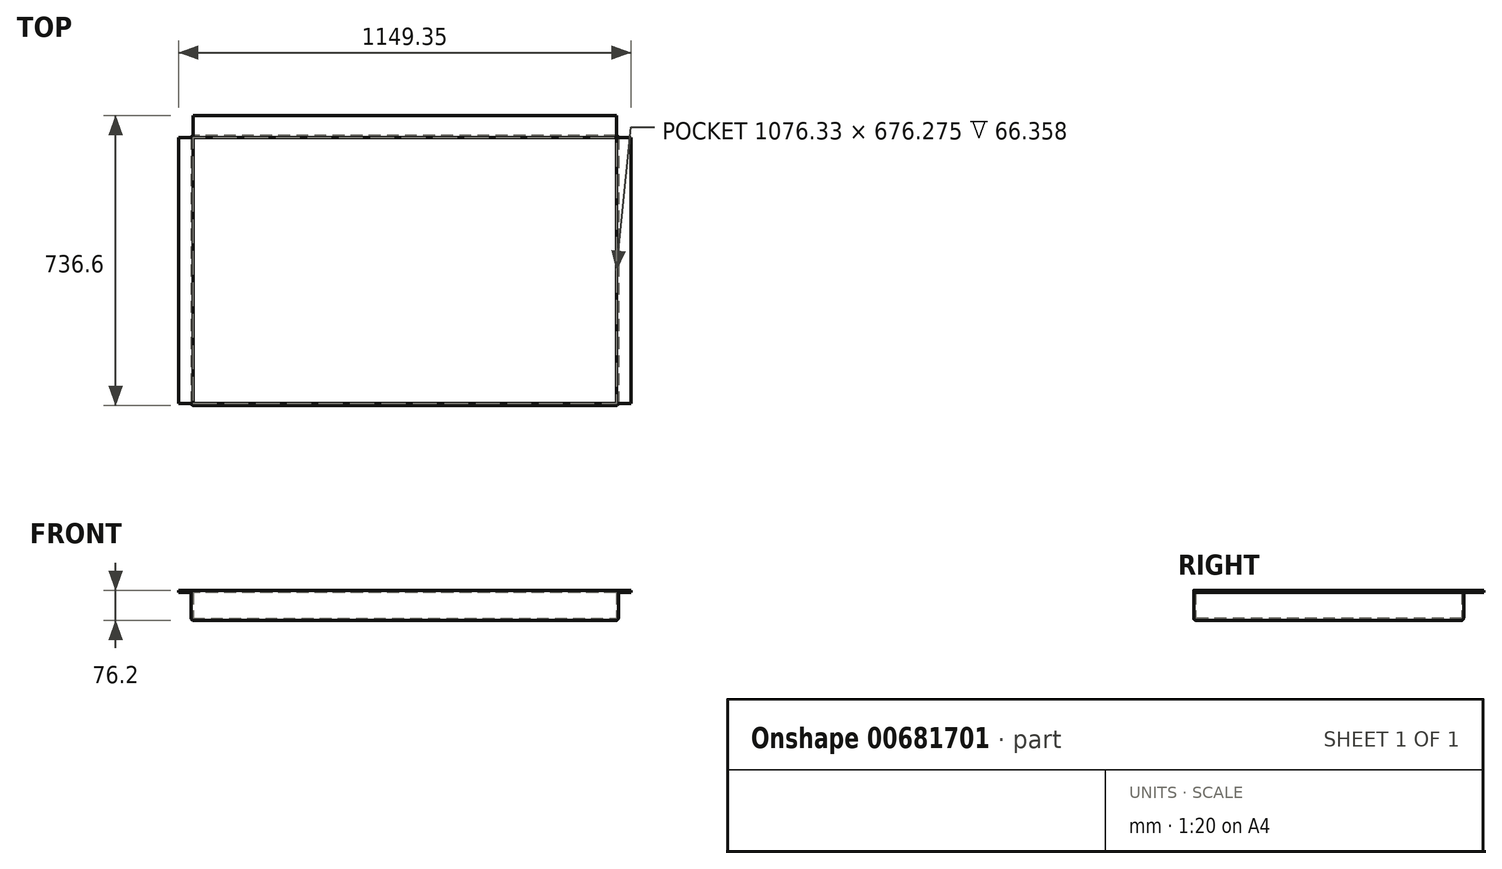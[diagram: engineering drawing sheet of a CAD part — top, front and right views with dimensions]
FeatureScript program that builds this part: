
annotation { "Feature Type Name" : "Feature", "Feature Type Description" : "" }
export const myFeature = defineFeature(function(context is Context, id is Id, definition is map)
    precondition{}
    {
        {
            var Q0;
            Q0=qCreatedBy(makeId("Top.planeOp"),FACE);
            var sketch = newSketch(context, id + "F0", { "sketchPlane" : qUnion([Q0])});
            skLineSegment(sketch, "E0.bottom", {"start": v(-1085.85, 685.8) * mm, "end": v(0, 685.8) * mm});
            skLineSegment(sketch, "E0.top", {"start": v(-1085.85, 0) * mm, "end": v(0, 0) * mm});
            skLineSegment(sketch, "E0.left", {"start": v(-1085.85, 685.8) * mm, "end": v(-1085.85, 0) * mm});
            skLineSegment(sketch, "E0.right", {"start": v(0, 685.8) * mm, "end": v(0, 0) * mm});
            skSolve(sketch);
        }
        {
            var Q0;
            Q0=makeQuery(id+"F0.imprint","IMPRINT",FACE,{"disambiguationData":[TD([[makeQuery(id+"F0.imprint","IMPRINT",EDGE,{"derivedFrom":sQuery(id+"F0.wireOp",EDGE,"E0.bottom")}),-1.0]])]});
            extrude(context, id + "F1", {"entities" : qUnion([Q0]), "depth" : 76.2 * mm, "offsetDistance" : 25.4 * mm});
        }
        {
            var Q0;
            Q0=makeQuery(id+"F8.boolean.opBoolean","MERGE",FACE,{"derivedFrom":[makeQuery(id+"F6.boolean.opBoolean","MERGE",FACE,{"derivedFrom":[makeQuery(id+"F4.boolean.opBoolean","MERGE",FACE,{"derivedFrom":[makeQuery(id+"F1.opExtrude","CAP_FACE",FACE,{"disambiguationData":[OSD([sQuery(id+"F0.wireOp",EDGE,"E0.bottom"),sQuery(id+"F0.wireOp",EDGE,"E0.top"),sQuery(id+"F0.wireOp",EDGE,"E0.left"),sQuery(id+"F0.wireOp",EDGE,"E0.right")])],"isStart":false}),makeQuery(id+"F4.opExtrude","SWEPT_FACE",FACE,{"disambiguationData":[OSD([sQuery(id+"F3.wireOp",EDGE,"44d1248c-61a8-45d5-8632-d3e4858e4744.0.2")])]})]}),makeQuery(id+"F6.opExtrude","SWEPT_FACE",FACE,{"disambiguationData":[OSD([sQuery(id+"F5.wireOp",EDGE,"3c0d171c-9aaa-4276-868c-e9e233a4677e.0.2")])]})]}),makeQuery(id+"F8.opExtrude","SWEPT_FACE",FACE,{"disambiguationData":[OSD([sQuery(id+"F7.wireOp",EDGE,"b2a400e3-6624-437d-8caf-46d41290d6b5.1.7")])]})]});
            shell(context, id + "F2", {"entities" : qUnion([Q0]), "thickness" : 4.76 * mm});
        }
        {
            var Q0;
            Q0=makeQuery(id+"F1.opExtrude","SWEPT_FACE",FACE,{"disambiguationData":[OSD([sQuery(id+"F0.wireOp",EDGE,"E0.left")])]});
            var sketch = newSketch(context, id + "F3", { "sketchPlane" : qUnion([Q0])});
            skLineSegment(sketch, "E1.0.0", {"start": v(-4.76, 4.76) * mm, "end": v(-681.04, 4.76) * mm});
            skLineSegment(sketch, "E1.0.1", {"start": v(-681.04, 4.76) * mm, "end": v(-681.04, 76.2) * mm});
            skLineSegment(sketch, "E1.0.2", {"start": v(-681.04, 76.2) * mm, "end": v(-4.76, 76.2) * mm});
            skLineSegment(sketch, "E1.0.3", {"start": v(-4.76, 76.2) * mm, "end": v(-4.76, 4.76) * mm});
            skLineSegment(sketch, "E2", {"start": v(-681.04, 71.44) * mm, "end": v(-4.76, 71.44) * mm});
            skSolve(sketch);
        }
        {
            var Q0;
            {var subQ0=sQuery(id+"F3.wireOp",EDGE,"E1.0.2");Q0=makeQuery(id+"F3.imprint","IMPRINT",FACE,{"disambiguationData":[TD([[makeQuery(id+"F3.imprint","IMPRINT",EDGE,{"derivedFrom":subQ0}),-1.0]])]});}
            extrude(context, id + "F4", {"entities" : qUnion([Q0]), "operationType" : NewBodyOperationType.ADD, "depth" : 31.75 * mm, "offsetDistance" : 25.4 * mm});
        }
        {
            var Q0;
            Q0=makeQuery(id+"F1.opExtrude","SWEPT_FACE",FACE,{"disambiguationData":[OSD([sQuery(id+"F0.wireOp",EDGE,"E0.right")])]});
            var sketch = newSketch(context, id + "F5", { "sketchPlane" : qUnion([Q0])});
            skLineSegment(sketch, "E3.0.0", {"start": v(681.04, 4.76) * mm, "end": v(4.76, 4.76) * mm});
            skLineSegment(sketch, "E3.0.1", {"start": v(4.76, 4.76) * mm, "end": v(4.76, 76.2) * mm});
            skLineSegment(sketch, "E3.0.2", {"start": v(4.76, 76.2) * mm, "end": v(681.04, 76.2) * mm});
            skLineSegment(sketch, "E3.0.3", {"start": v(681.04, 76.2) * mm, "end": v(681.04, 4.76) * mm});
            skLineSegment(sketch, "E4", {"start": v(4.76, 71.44) * mm, "end": v(681.04, 71.44) * mm});
            skPoint(sketch, "E4.endSnap0", {"position": v(681.04, 40.48) * mm});
            skSolve(sketch);
        }
        {
            var Q0;
            {var subQ0=sQuery(id+"F5.wireOp",EDGE,"E3.0.2");Q0=makeQuery(id+"F5.imprint","IMPRINT",FACE,{"disambiguationData":[TD([[makeQuery(id+"F5.imprint","IMPRINT",EDGE,{"derivedFrom":subQ0}),1.0]])]});}
            extrude(context, id + "F6", {"entities" : qUnion([Q0]), "operationType" : NewBodyOperationType.ADD, "depth" : 31.75 * mm, "offsetDistance" : 25.4 * mm});
        }
        {
            var Q0;
            Q0=makeQuery(id+"F1.opExtrude","SWEPT_FACE",FACE,{"disambiguationData":[OSD([sQuery(id+"F0.wireOp",EDGE,"E0.bottom")])]});
            var sketch = newSketch(context, id + "F7", { "sketchPlane" : qUnion([Q0])});
            skLineSegment(sketch, "E5.0.0", {"start": v(1081.09, 4.76) * mm, "end": v(4.76, 4.76) * mm});
            skLineSegment(sketch, "E5.0.1", {"start": v(4.76, 4.76) * mm, "end": v(4.76, 76.2) * mm});
            skLineSegment(sketch, "E5.0.2", {"start": v(4.76, 76.2) * mm, "end": v(1081.09, 76.2) * mm});
            skLineSegment(sketch, "E5.0.3", {"start": v(1081.09, 76.2) * mm, "end": v(1081.09, 4.76) * mm});
            skLineSegment(sketch, "E6", {"start": v(4.76, 71.44) * mm, "end": v(1081.09, 71.44) * mm});
            skSolve(sketch);
        }
        {
            var Q0;
            {var subQ0=sQuery(id+"F7.wireOp",EDGE,"E5.0.2");Q0=makeQuery(id+"F7.imprint","IMPRINT",FACE,{"disambiguationData":[TD([[makeQuery(id+"F7.imprint","IMPRINT",EDGE,{"derivedFrom":subQ0}),1.0]])]});}
            extrude(context, id + "F8", {"entities" : qUnion([Q0]), "operationType" : NewBodyOperationType.ADD, "depth" : 50.8 * mm, "offsetDistance" : 25.4 * mm});
        }
        {
            var Q0;
            Q0=makeQuery(id+"F1.opExtrude","CAP_FACE",FACE,{"disambiguationData":[OSD([sQuery(id+"F0.wireOp",EDGE,"E0.bottom"),sQuery(id+"F0.wireOp",EDGE,"E0.top"),sQuery(id+"F0.wireOp",EDGE,"E0.left"),sQuery(id+"F0.wireOp",EDGE,"E0.right")])],"isStart":true});
            var Q1;
            Q1=makeQuery(id+"F1.opExtrude","SWEPT_EDGE",EDGE,{"disambiguationData":[OSD([sQuery(id+"F0.wireOp",EDGE,"E0.bottom"),sQuery(id+"F0.wireOp",EDGE,"E0.left")])]});
            var Q2;
            Q2=makeQuery(id+"F1.opExtrude","SWEPT_EDGE",EDGE,{"disambiguationData":[OSD([sQuery(id+"F0.wireOp",EDGE,"E0.top"),sQuery(id+"F0.wireOp",EDGE,"E0.left")])]});
            var Q3;
            Q3=makeQuery(id+"F1.opExtrude","SWEPT_EDGE",EDGE,{"disambiguationData":[OSD([sQuery(id+"F0.wireOp",EDGE,"E0.top"),sQuery(id+"F0.wireOp",EDGE,"E0.right")])]});
            var Q4;
            Q4=makeQuery(id+"F1.opExtrude","SWEPT_EDGE",EDGE,{"disambiguationData":[OSD([sQuery(id+"F0.wireOp",EDGE,"E0.bottom"),sQuery(id+"F0.wireOp",EDGE,"E0.right")])]});
            fillet(context, id + "F9", {"entities" : qUnion([Q0, Q1, Q2, Q3, Q4]), "radius" : 6.35 * mm, "tangentPropagation" : true, "allowEdgeOverflow" : false});
        }
        {
            var Q0;
            {var subQ0=sQuery(id+"F0.wireOp",EDGE,"E0.bottom");Q0=makeQuery(id+"F2.opShell","OFFSET_EDGE",EDGE,{"disambiguationData":[OSD([subQ0]),TDD([makeQuery(id+"F1.opExtrude","CAP_EDGE",EDGE,{"disambiguationData":[OSD([subQ0])],"isStart":false})])]});}
            var Q1;
            {var subQ0=sQuery(id+"F0.wireOp",EDGE,"E0.left");Q1=makeQuery(id+"F2.opShell","OFFSET_EDGE",EDGE,{"disambiguationData":[OSD([subQ0]),TDD([makeQuery(id+"F1.opExtrude","CAP_EDGE",EDGE,{"disambiguationData":[OSD([subQ0])],"isStart":false})])]});}
            var Q2;
            {var subQ0=sQuery(id+"F0.wireOp",EDGE,"E0.right");Q2=makeQuery(id+"F2.opShell","OFFSET_EDGE",EDGE,{"disambiguationData":[OSD([subQ0]),TDD([makeQuery(id+"F1.opExtrude","CAP_EDGE",EDGE,{"disambiguationData":[OSD([subQ0])],"isStart":false})])]});}
            fillet(context, id + "F10", {"entities" : qUnion([Q0, Q1, Q2]), "radius" : 5.08 * mm, "tangentPropagation" : true, "allowEdgeOverflow" : false});
        }
    });
